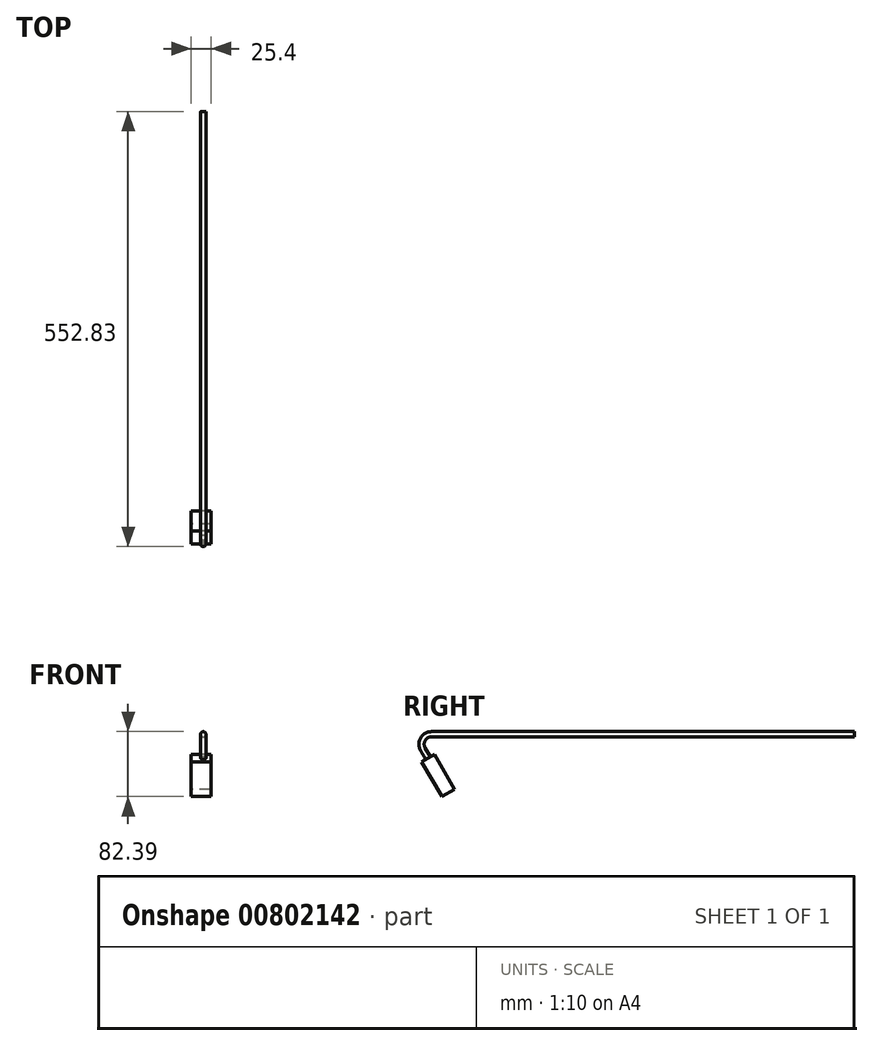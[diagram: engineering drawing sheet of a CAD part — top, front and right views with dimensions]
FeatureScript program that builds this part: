
annotation { "Feature Type Name" : "Feature", "Feature Type Description" : "" }
export const myFeature = defineFeature(function(context is Context, id is Id, definition is map)
    precondition{}
    {
        {
            var Q0;
            Q0=qCreatedBy(makeId("Right.planeOp"),FACE);
            var sketch = newSketch(context, id + "F0", { "sketchPlane" : qUnion([Q0])});
            skLineSegment(sketch, "E0", {"start": v(0, 0) * mm, "end": v(-25.4, 44) * mm});
            skLineSegment(sketch, "E1", {"start": v(-25.4, 44) * mm, "end": v(-41.46, 34.72) * mm});
            skLineSegment(sketch, "E2", {"start": v(-41.46, 34.72) * mm, "end": v(-16.06, -9.27) * mm});
            skLineSegment(sketch, "E3", {"start": v(-16.06, -9.27) * mm, "end": v(0, 0) * mm});
            skLineSegment(sketch, "E4", {"start": v(0, 0) * mm, "end": v(0, -57.51) * mm, "construction": true});
            skSolve(sketch);
        }
        {
            var Q0;
            Q0=qSketchRegion(id+"F0",true);
            extrude(context, id + "F1", {"entities" : qUnion([Q0]), "depth" : 25.4 * mm});
        }
        {
            var Q0;
            Q0=qCreatedBy(makeId("Right.planeOp"),FACE);
            cPlane(context, id + "F2", {"entities" : qUnion([Q0]), "cplaneType" : CPlaneType.OFFSET, "offset" : 15.24 * mm, "width" : 152.4 * mm, "height" : 152.4 * mm});
        }
        {
            var Q0;
            Q0=qCreatedBy(id+"F2.planeOp",FACE);
            var sketch = newSketch(context, id + "F3", { "sketchPlane" : qUnion([Q0])});
            skLineSegment(sketch, "E5", {"start": v(-33.43, 39.36) * mm, "end": v(-40, 50.74) * mm});
            skLineSegment(sketch, "E6", {"start": v(-29, 69.79) * mm, "end": v(507.8, 69.79) * mm});
            skPoint(sketch, "E7.visualSharp", {"position": v(-51, 69.79) * mm});
            skArc(sketch, "E7.filletArc", {"start": v(-29, 69.79) * mm, "mid": v(-40, 63.44) * mm, "end": v(-40, 50.74) * mm});
            skSolve(sketch);
        }
        {
            var Q0;
            Q0=makeQuery(id+"F1.opExtrude","SWEPT_FACE",FACE,{"disambiguationData":[OSD([sQuery(id+"F0.wireOp",EDGE,"E1")])]});
            var sketch = newSketch(context, id + "F4", { "sketchPlane" : qUnion([Q0])});
            skCircle(sketch, "E8", {"center": v(15.24, -9.27) * mm, "radius": 3.33 * mm});
            skSolve(sketch);
        }
        {
            var Q0;
            Q0=qSketchRegion(id+"F4",true);
            var Q1;
            Q1=qConstructionFilter(qBodyType(qCreatedBy(id+"F3",EDGE),BodyType.WIRE),ConstructionObject.NO);
            sweep(context, id + "F5", {"operationType" : NewBodyOperationType.ADD, "profiles" : qUnion([Q0]), "path" : qUnion([Q1])});
        }
    });
